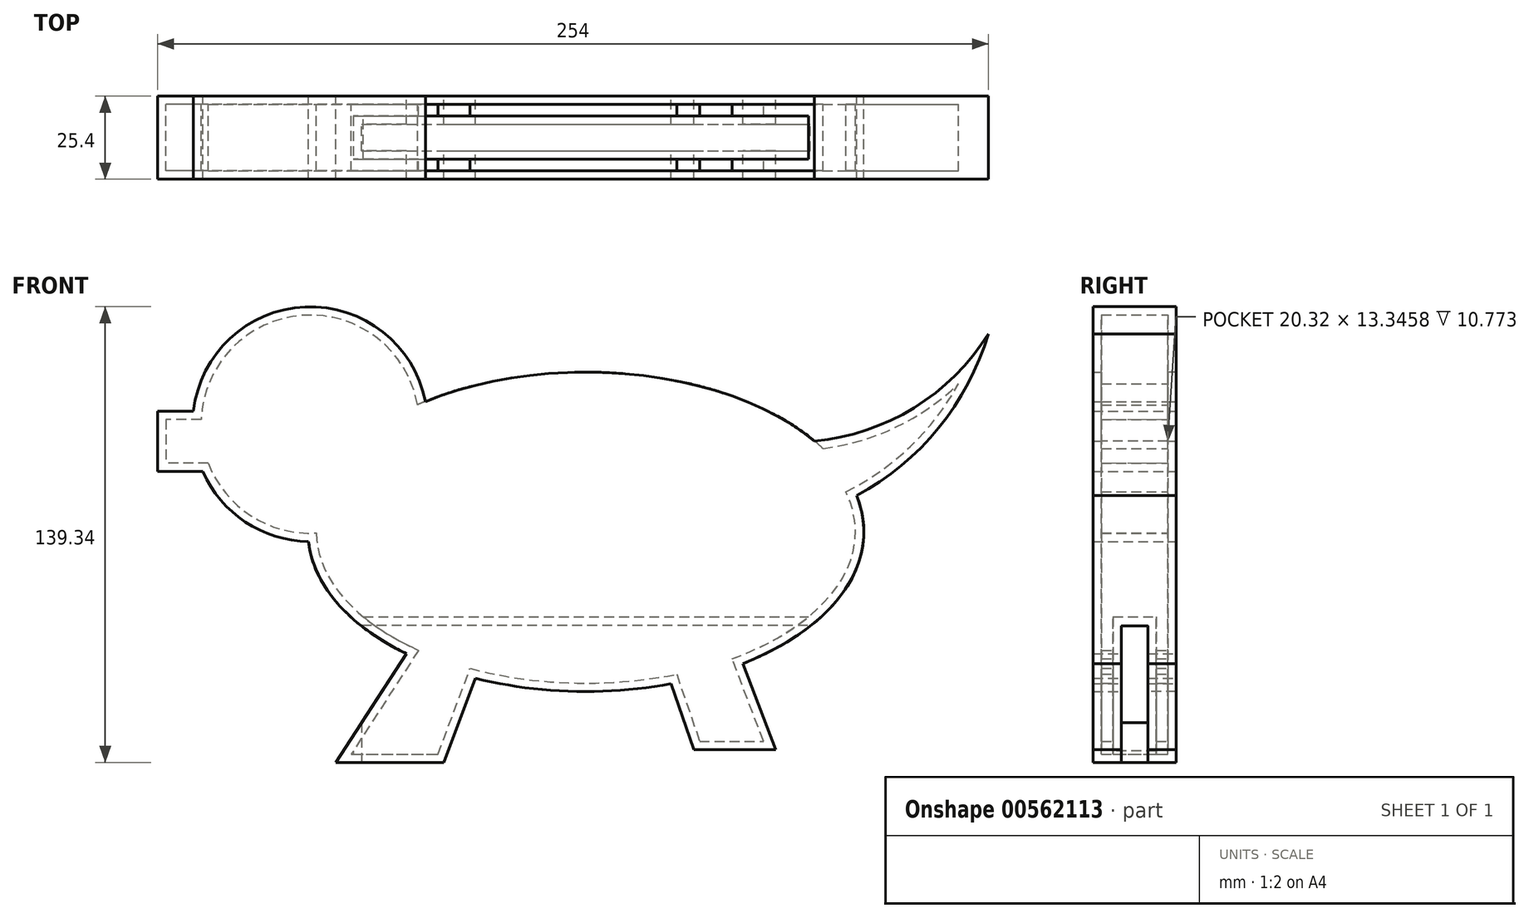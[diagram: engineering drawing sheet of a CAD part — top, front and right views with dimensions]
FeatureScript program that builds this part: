
annotation { "Feature Type Name" : "Feature", "Feature Type Description" : "" }
export const myFeature = defineFeature(function(context is Context, id is Id, definition is map)
    precondition{}
    {
        {
            var Q0;
            Q0=qCreatedBy(makeId("Front.planeOp"),FACE);
            var sketch = newSketch(context, id + "F0", { "sketchPlane" : qUnion([Q0])});
            skArc(sketch, "E0", {"start": v(-49.1, 60.27) * mm, "mid": v(-85.8, 89.2) * mm, "end": v(-119.98, 57.3) * mm});
            skLineSegment(sketch, "E1.bottom", {"start": v(-119.98, 57.3) * mm, "end": v(-130.94, 57.3) * mm});
            skLineSegment(sketch, "E1.top", {"start": v(-117.15, 38.88) * mm, "end": v(-130.94, 38.88) * mm});
            skLineSegment(sketch, "E1.right", {"start": v(-130.94, 57.3) * mm, "end": v(-130.94, 38.88) * mm});
            skPoint(sketch, "E1.middle", {"position": v(-119.8, 48.09) * mm});
            skEllipticalArc(sketch, "E2", {});
            skLineSegment(sketch, "E3", {"start": v(-54.87, -16.86) * mm, "end": v(-76.43, -50.1) * mm});
            skLineSegment(sketch, "E4", {"start": v(-76.43, -50.1) * mm, "end": v(-43.47, -50.1) * mm});
            skLineSegment(sketch, "E5", {"start": v(-43.47, -50.1) * mm, "end": v(-33.82, -24.38) * mm});
            skLineSegment(sketch, "E6", {"start": v(26.06, -26.06) * mm, "end": v(32.94, -46.15) * mm});
            skLineSegment(sketch, "E7", {"start": v(32.94, -46.15) * mm, "end": v(57.96, -46.15) * mm});
            skLineSegment(sketch, "E8", {"start": v(57.96, -46.15) * mm, "end": v(47.97, -19.88) * mm});
            skArc(sketch, "E9", {"start": v(69.9, 48.18) * mm, "mid": v(100.33, 58.34) * mm, "end": v(123.06, 80.98) * mm});
            skArc(sketch, "E10", {"start": v(82.77, 31.46) * mm, "mid": v(107.85, 52.2) * mm, "end": v(123.06, 80.98) * mm});
            skPoint(sketch, "E11.orphan", {"position": v(-108.68, 57.3) * mm});
            skPoint(sketch, "E12.orphan", {"position": v(-108.68, 38.88) * mm});
            skArc(sketch, "E13.trimOffspring", {"start": v(-117.15, 38.88) * mm, "mid": v(-104.12, 23.43) * mm, "end": v(-84.81, 17.47) * mm});
            skEllipticalArc(sketch, "E14.trimOffspring", {});
            skEllipticalArc(sketch, "E15.trimOffspring", {});
            skEllipticalArc(sketch, "E16.trimOffspring", {});
            const initialGuessF0  = {"E2": [0, 0.02041815501646871, 1, 0, 0.08496587226785601, 0.04883003868821765, 3.2021015271119455, 4.010294762718546], "E14.trimOffspring": [0, 0.02041815501646871, 1, 0, 0.08496587226785601, 0.04883003868821765, 4.30304403206738, 5.024111056175922], "E15.trimOffspring": [0, 0.02041815501646871, 1, 0, 0.08496587226785601, 0.04883003868821765, 5.312366757467492, 0.22801741398875394], "E16.trimOffspring": [0, 0.02041815501646871, 1, 0, 0.08496587226785601, 0.04883003868821765, 0.6047898254051107, 2.186811249648626]};
            skSetInitialGuess(sketch, initialGuessF0);
            skSolve(sketch);
        }
        {
            var Q0;
            Q0 = qSketchRegion(id + "F0", true);
            extrude(context, id + "F1", {"entities" : qUnion([Q0]), "endBound" : BoundingType.SYMMETRIC, "depth" : 25.4 * mm, "offsetDistance" : 25.4 * mm});
        }
        {
            var Q0;
            Q0=qCreatedBy(makeId("Right.planeOp"),FACE);
            var sketch = newSketch(context, id + "F2", { "sketchPlane" : qUnion([Q0])});
            skLineSegment(sketch, "E17.bottom", {"start": v(-4.06, -8.13) * mm, "end": v(4.06, -8.13) * mm});
            skLineSegment(sketch, "E17.top", {"start": v(-4.06, -63.76) * mm, "end": v(4.06, -63.76) * mm});
            skLineSegment(sketch, "E17.left", {"start": v(-4.06, -8.13) * mm, "end": v(-4.06, -63.76) * mm});
            skLineSegment(sketch, "E17.right", {"start": v(4.06, -8.13) * mm, "end": v(4.06, -63.76) * mm});
            skPoint(sketch, "E17.middle", {"position": v(0, -35.94) * mm});
            skSolve(sketch);
        }
        {
            var Q0;
            Q0 = qSketchRegion(id + "F2", true);
            extrude(context, id + "F3", {"entities" : qUnion([Q0]), "operationType" : NewBodyOperationType.REMOVE, "endBound" : BoundingType.SYMMETRIC, "oppositeDirection" : true, "depth" : 137.16 * mm, "offsetDistance" : 25.4 * mm});
        }
        {
            var Q0;
            Q0=makeQuery(id+"F1.opExtrude","SWEPT_FACE",FACE,{"disambiguationData":[OSD([sQuery(id+"F0.wireOp",EDGE,"E16.trimOffspring")])]});
            shell(context, id + "F4", {"entities" : qUnion([Q0]), "thickness" : 2.54 * mm});
        }
    });
